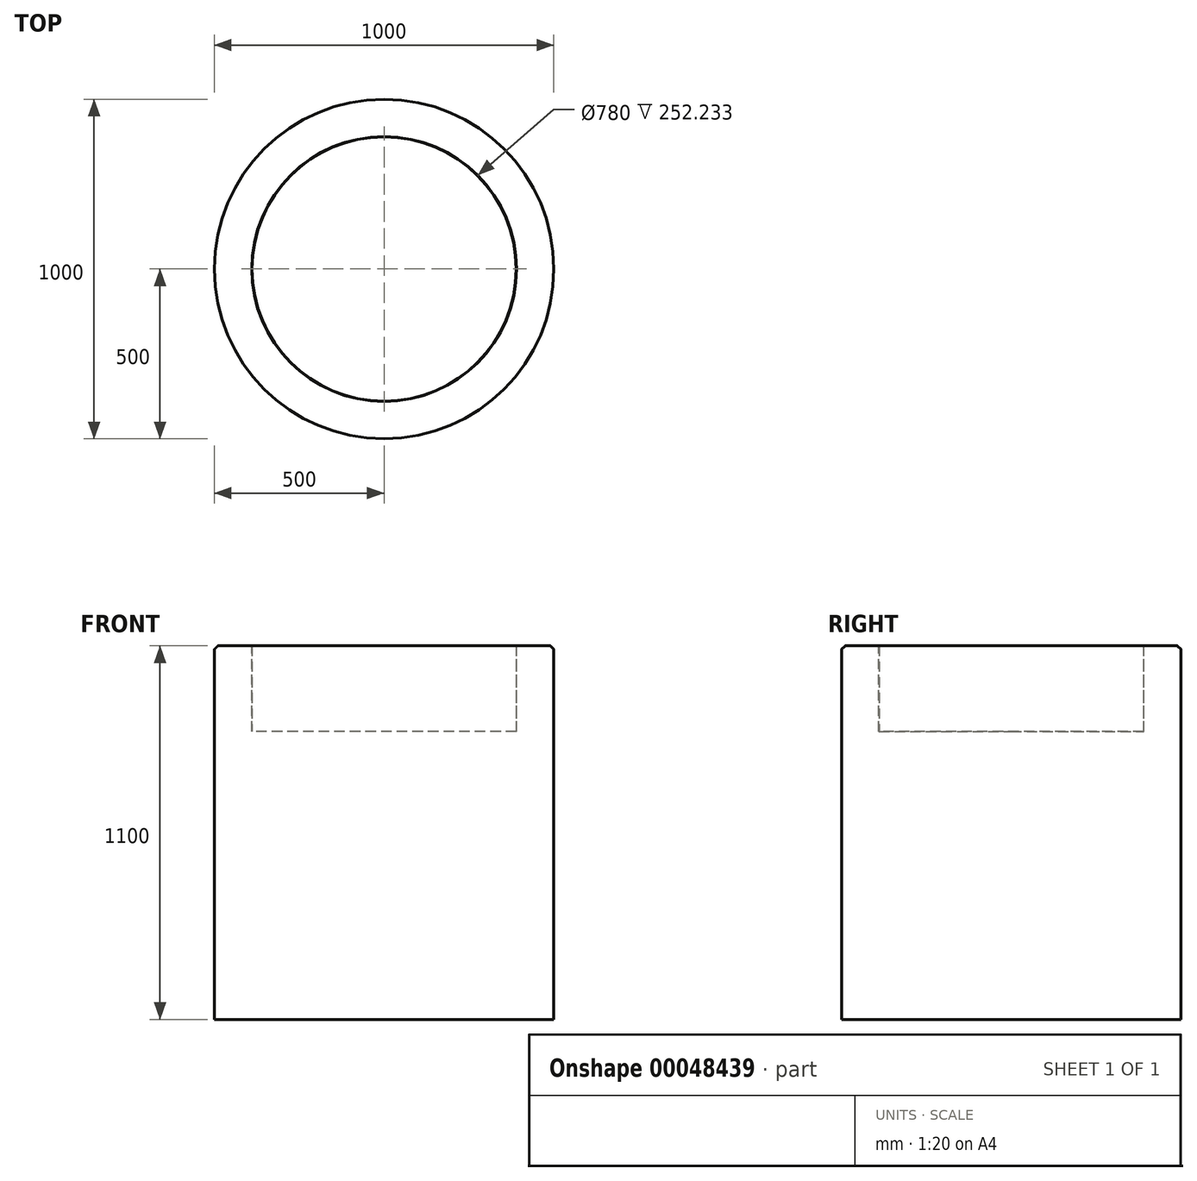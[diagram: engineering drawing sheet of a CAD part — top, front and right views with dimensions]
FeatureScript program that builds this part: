
annotation { "Feature Type Name" : "Feature", "Feature Type Description" : "" }
export const myFeature = defineFeature(function(context is Context, id is Id, definition is map)
    precondition{}
    {
        {
            var Q0;
            Q0=qCreatedBy(makeId("Top.planeOp"),FACE);
            var sketch = newSketch(context, id + "F0", { "sketchPlane" : qUnion([Q0])});
            skCircle(sketch, "E0", {"center": v(0, 0) * mm, "radius": 500 * mm});
            skSolve(sketch);
        }
        {
            var Q0;
            Q0 = qSketchRegion(id + "F0", true);
            extrude(context, id + "F1", {"entities" : qUnion([Q0]), "depth" : 1100 * mm});
        }
        {
            var Q0;
            Q0=makeQuery(id+"F1.opExtrude","CAP_EDGE",EDGE,{"disambiguationData":[OSD([sQuery(id+"F0.wireOp",EDGE,"E0")])],"isStart":false});
            chamfer(context, id + "F2", {"entities" : qUnion([Q0]), "width" : 10 * mm, "tangentPropagation" : true});
        }
        {
            var Q0;
            Q0=makeQuery(id+"F1.opExtrude","CAP_FACE",FACE,{"disambiguationData":[OSD([sQuery(id+"F0.wireOp",EDGE,"E0")])],"isStart":false});
            var sketch = newSketch(context, id + "F3", { "sketchPlane" : qUnion([Q0])});
            skCircle(sketch, "E1", {"center": v(0, 0) * mm, "radius": 390 * mm});
            skSolve(sketch);
        }
        {
            var Q0;
            Q0=makeQuery(id+"F3.imprint","IMPRINT",FACE,{"disambiguationData":[TD([[makeQuery(id+"F3.imprint","IMPRINT",EDGE,{"derivedFrom":sQuery(id+"F3.wireOp",EDGE,"E1")}),1.0]])]});
            extrude(context, id + "F4", {"entities" : qUnion([Q0]), "operationType" : NewBodyOperationType.REMOVE, "oppositeDirection" : true, "depth" : 252.23 * mm});
        }
        {
            var Q0;
            Q0=makeQuery(id+"F4.boolean.opBoolean","COPY",FACE,{"derivedFrom":makeQuery(id+"F4.opExtrude","CAP_FACE",FACE,{"disambiguationData":[OSD([sQuery(id+"F3.wireOp",EDGE,"E1")])],"isStart":false})});
            var sketch = newSketch(context, id + "F5", { "sketchPlane" : qUnion([Q0])});
            skCircle(sketch, "E2", {"center": v(0, 0) * mm, "radius": 389 * mm});
            skSolve(sketch);
        }
        {
            var Q0;
            Q0=makeQuery(id+"F5.imprint","IMPRINT",FACE,{"disambiguationData":[TD([[makeQuery(id+"F5.imprint","IMPRINT",EDGE,{"derivedFrom":sQuery(id+"F5.wireOp",EDGE,"E2")}),1.0]])]});
            var Q1;
            Q1=makeQuery(id+"F1.opExtrude","CAP_FACE",FACE,{"disambiguationData":[OSD([sQuery(id+"F0.wireOp",EDGE,"E0")])],"isStart":false});
            extrude(context, id + "F6", {"entities" : qUnion([Q0]), "endBound" : BoundingType.UP_TO_SURFACE, "endBoundEntityFace" : qUnion([Q1]), "depth" : 25 * mm});
        }
        {
            var Q0;
            Q0=makeQuery(id+"F6.opExtrude","CAP_EDGE",EDGE,{"disambiguationData":[OSD([sQuery(id+"F5.wireOp",EDGE,"E2")])],"isStart":false});
            fillet(context, id + "F7", {"entities" : qUnion([Q0]), "radius" : .2 * mm, "tangentPropagation" : true, "allowEdgeOverflow" : false});
        }
        {
            var Q0;
            Q0=makeQuery(id+"F4.boolean.opBoolean","COPY",EDGE,{"derivedFrom":makeQuery(id+"F4.opExtrude","CAP_EDGE",EDGE,{"disambiguationData":[OSD([sQuery(id+"F3.wireOp",EDGE,"E1")])],"isStart":true})});
            var Q1;
            {var subQ0=sQuery(id+"F0.wireOp",EDGE,"E0");Q1=makeQuery(id+"F2.opChamfer","BLEND_EDGE",EDGE,{"blendedFrom":[makeQuery(id+"F1.opExtrude","CAP_EDGE",EDGE,{"disambiguationData":[OSD([subQ0])],"isStart":false}),makeQuery(id+"F1.opExtrude","CAP_FACE",FACE,{"disambiguationData":[OSD([subQ0])],"isStart":false})],"blendedInto":[makeQuery(id+"F1.opExtrude","CAP_FACE",FACE,{"disambiguationData":[OSD([subQ0])],"isStart":false})]});}
            var Q2;
            {var subQ0=sQuery(id+"F0.wireOp",EDGE,"E0");Q2=makeQuery(id+"F2.opChamfer","BLEND_EDGE",EDGE,{"blendedFrom":[makeQuery(id+"F1.opExtrude","CAP_EDGE",EDGE,{"disambiguationData":[OSD([subQ0])],"isStart":false}),makeQuery(id+"F1.opExtrude","SWEPT_FACE",FACE,{"disambiguationData":[OSD([subQ0])]})],"blendedInto":[makeQuery(id+"F1.opExtrude","SWEPT_FACE",FACE,{"disambiguationData":[OSD([subQ0])]})]});}
            fillet(context, id + "F8", {"entities" : qUnion([Q0, Q1, Q2]), "radius" : .2 * mm, "tangentPropagation" : true, "allowEdgeOverflow" : false});
        }
    });
